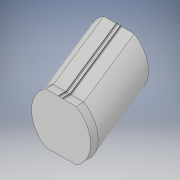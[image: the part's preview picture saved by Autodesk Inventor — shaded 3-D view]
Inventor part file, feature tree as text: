
AUTODESK INVENTOR PART (.ipt)
format: ipt  version: 2017 (Build 210142000, 142)  size: 179,200 bytes
history: native  units: in
note: dims shown in document units (in); Inventor stores cm internally (conversion verified against a paired STEP export)
features: sketch x2, plane x1, sweep x1, extrude x1
ambient origin geometry x8: Origin, YZ Plane, XZ Plane, XY Plane, X Axis, Y Axis, Z Axis, Center Point
bodies: Solid1 (feature_tree)
feature tree (5):
  sketch  "Sketch1"  dims[d0=6.6667in d28=8.0in]
  plane  "Work Plane2"
  sweep  "ramp"
  extrude  "connection bottom"  Depth=0.0892in TaperAngle=0.0deg
  sketch  "Sketch6"  dims[d30=0.0in d31=0.0in d32=1.0in d33=0.0in d62=0.8521in d110=4.0in d111=0.5833in d112=3.8873in d113=3.8873in d114=1.7083in d115=0.0625in d116=0.0625in d117=1.6458in d118=0.25in d119=0.125in d120=0.0892in d121=0.0884in d122=45.0deg d123=3.3333in d124=0.125in d125=4.0in d126=0.5833in d127=3.8873in d128=3.8873in d129=1.7083in d130=0.0625in d131=0.0625in d132=1.6458in d133=0.25in d134=0.125in d135=0.0892in d136=0.0884in d137=45.0deg d138=3.3333in d139=0.125in]
